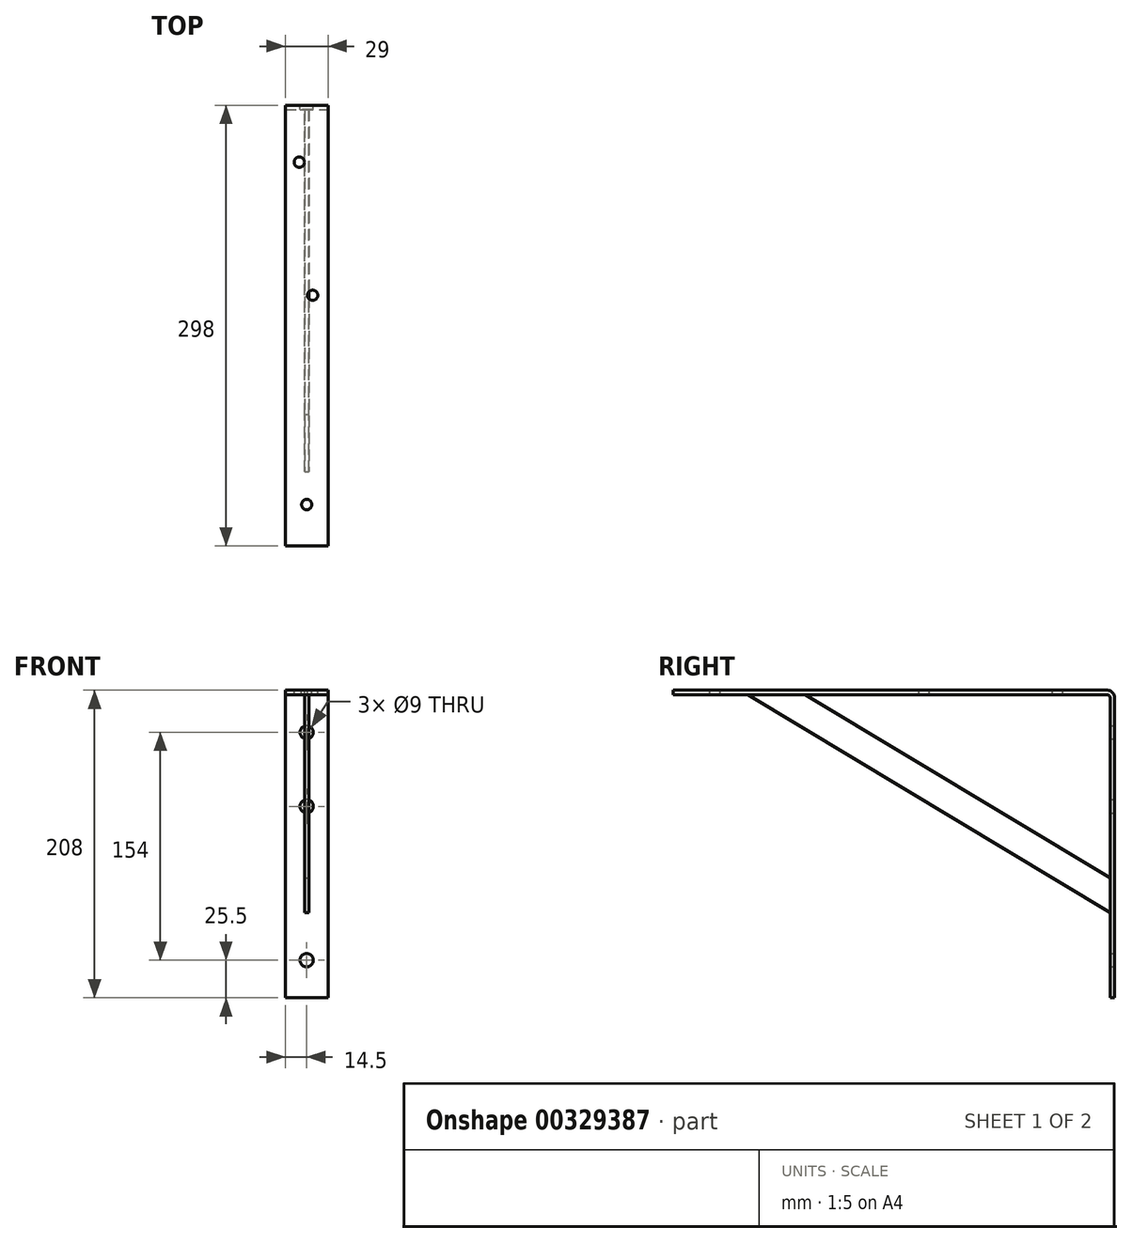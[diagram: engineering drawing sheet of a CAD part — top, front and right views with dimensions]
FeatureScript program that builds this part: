
annotation { "Feature Type Name" : "Feature", "Feature Type Description" : "" }
export const myFeature = defineFeature(function(context is Context, id is Id, definition is map)
    precondition{}
    {
        {
            var Q0;
            Q0=qCreatedBy(makeId("Right.planeOp"),FACE);
            var sketch = newSketch(context, id + "F0", { "sketchPlane" : qUnion([Q0])});
            skLineSegment(sketch, "E0", {"start": v(-298, 0) * mm, "end": v(-5, 0) * mm});
            skLineSegment(sketch, "E1", {"start": v(0, -5) * mm, "end": v(0, -208) * mm});
            skPoint(sketch, "E2.visualSharp", {"position": v(0, 0) * mm});
            skArc(sketch, "E2.filletArc", {"start": v(0, -5) * mm, "mid": v(-1.46, -1.46) * mm, "end": v(-5, 0) * mm});
            skLineSegment(sketch, "E3.0", {"start": v(-3, -5) * mm, "end": v(-3, -208) * mm});
            skLineSegment(sketch, "E3.1", {"start": v(-298, -3) * mm, "end": v(-5, -3) * mm});
            skPoint(sketch, "E4.visualSharp", {"position": v(-3, -3) * mm});
            skArc(sketch, "E4.filletArc", {"start": v(-3, -5) * mm, "mid": v(-3.59, -3.59) * mm, "end": v(-5, -3) * mm});
            skLineSegment(sketch, "E5", {"start": v(-3, -208) * mm, "end": v(0, -208) * mm});
            skLineSegment(sketch, "E6", {"start": v(-298, -3) * mm, "end": v(-298, 0) * mm});
            skSolve(sketch);
        }
        {
            var Q0;
            Q0 = qSketchRegion(id + "F0", true);
            extrude(context, id + "F1", {"entities" : qUnion([Q0]), "endBound" : BoundingType.SYMMETRIC, "oppositeDirection" : true, "depth" : 29 * mm});
        }
        {
            var Q0;
            Q0=qCreatedBy(makeId("Right.planeOp"),FACE);
            var sketch = newSketch(context, id + "F2", { "sketchPlane" : qUnion([Q0])});
            skLineSegment(sketch, "E7", {"start": v(-3, -127) * mm, "end": v(-3, -150.34) * mm});
            skLineSegment(sketch, "E8", {"start": v(-3, -150.34) * mm, "end": v(-247.78, -3) * mm});
            skLineSegment(sketch, "E9", {"start": v(-247.78, -3) * mm, "end": v(-209, -3) * mm});
            skLineSegment(sketch, "E10", {"start": v(-209, -3) * mm, "end": v(-3, -127) * mm});
            skSolve(sketch);
        }
        {
            var Q0;
            Q0 = qSketchRegion(id + "F2", true);
            extrude(context, id + "F3", {"entities" : qUnion([Q0]), "operationType" : NewBodyOperationType.ADD, "endBound" : BoundingType.SYMMETRIC, "oppositeDirection" : true, "depth" : 3 * mm});
        }
        {
            var Q0;
            Q0=makeQuery(id+"F1.opExtrude","SWEPT_FACE",FACE,{"disambiguationData":[OSD([sQuery(id+"F0.wireOp",EDGE,"E1")])]});
            var sketch = newSketch(context, id + "F4", { "sketchPlane" : qUnion([Q0])});
            skLineSegment(sketch, "E11", {"start": v(0, -208) * mm, "end": v(0, -5) * mm, "construction": true});
            skCircle(sketch, "E12", {"center": v(0, -28.5) * mm, "radius": 4.5 * mm});
            skCircle(sketch, "E13", {"center": v(0, -78.5) * mm, "radius": 4.5 * mm});
            skCircle(sketch, "E14", {"center": v(0, -182.5) * mm, "radius": 4.5 * mm});
            skSolve(sketch);
        }
        {
            var Q0;
            Q0 = qSketchRegion(id + "F4", true);
            extrude(context, id + "F5", {"entities" : qUnion([Q0]), "operationType" : NewBodyOperationType.REMOVE, "oppositeDirection" : true, "depth" : 3 * mm});
        }
        {
            var Q0;
            Q0=makeQuery(id+"F1.opExtrude","SWEPT_FACE",FACE,{"disambiguationData":[OSD([sQuery(id+"F0.wireOp",EDGE,"E0")])]});
            var sketch = newSketch(context, id + "F6", { "sketchPlane" : qUnion([Q0])});
            skCircle(sketch, "E15", {"center": v(-5, -38.5) * mm, "radius": 3.5 * mm});
            skCircle(sketch, "E16", {"center": v(4, -128.5) * mm, "radius": 3.5 * mm});
            skCircle(sketch, "E17", {"center": v(0, -270) * mm, "radius": 3.5 * mm});
            skSolve(sketch);
        }
        {
            var Q0;
            Q0 = qSketchRegion(id + "F6", true);
            extrude(context, id + "F7", {"entities" : qUnion([Q0]), "operationType" : NewBodyOperationType.REMOVE, "oppositeDirection" : true, "depth" : 3 * mm});
        }
    });
